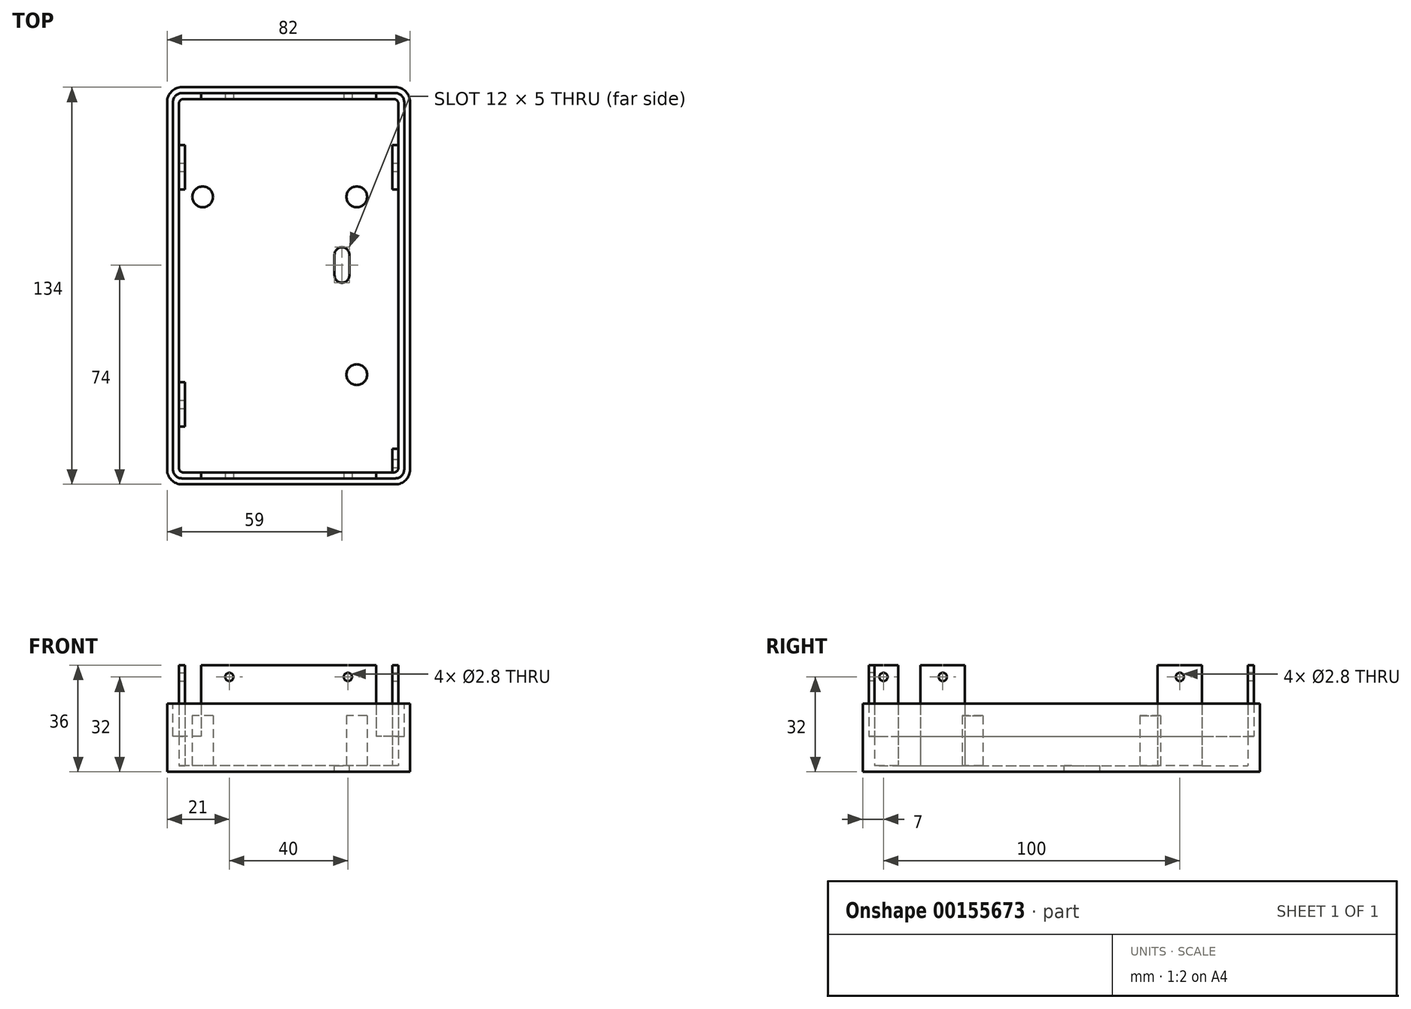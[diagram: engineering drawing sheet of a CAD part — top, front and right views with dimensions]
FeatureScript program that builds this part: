
annotation { "Feature Type Name" : "Feature", "Feature Type Description" : "" }
export const myFeature = defineFeature(function(context is Context, id is Id, definition is map)
    precondition{}
    {
        {
            var Q0;
            Q0=qCreatedBy(makeId("Top.planeOp"),FACE);
            var sketch = newSketch(context, id + "F0", { "sketchPlane" : qUnion([Q0])});
            skLineSegment(sketch, "E0.bottom", {"start": v(36, -67) * mm, "end": v(-36, -67) * mm});
            skLineSegment(sketch, "E0.top", {"start": v(36, 67) * mm, "end": v(-36, 67) * mm});
            skLineSegment(sketch, "E0.left", {"start": v(41, -62) * mm, "end": v(41, 62) * mm});
            skLineSegment(sketch, "E0.right", {"start": v(-41, -62) * mm, "end": v(-41, 62) * mm});
            skPoint(sketch, "E0.middle", {"position": v(0, 0) * mm});
            skPoint(sketch, "E1.visualSharp", {"position": v(-41, 67) * mm});
            skArc(sketch, "E1.filletArc", {"start": v(-36, 67) * mm, "mid": v(-39.54, 65.54) * mm, "end": v(-41, 62) * mm});
            skPoint(sketch, "E2.visualSharp", {"position": v(41, 67) * mm});
            skArc(sketch, "E2.filletArc", {"start": v(41, 62) * mm, "mid": v(39.54, 65.54) * mm, "end": v(36, 67) * mm});
            skPoint(sketch, "E3.visualSharp", {"position": v(41, -67) * mm});
            skArc(sketch, "E3.filletArc", {"start": v(36, -67) * mm, "mid": v(39.54, -65.54) * mm, "end": v(41, -62) * mm});
            skPoint(sketch, "E4.visualSharp", {"position": v(-41, -67) * mm});
            skArc(sketch, "E4.filletArc", {"start": v(-41, -62) * mm, "mid": v(-39.54, -65.54) * mm, "end": v(-36, -67) * mm});
            skSolve(sketch);
        }
        {
            var Q0;
            Q0=qSketchRegion(id+"F0",true);
            extrude(context, id + "F1", {"entities" : qUnion([Q0]), "depth" : 23 * mm});
        }
        {
            var Q0;
            Q0=makeQuery(id+"F1.opExtrude","CAP_FACE",FACE,{"disambiguationData":[OSD([sQuery(id+"F0.wireOp",EDGE,"E0.bottom"),sQuery(id+"F0.wireOp",EDGE,"E0.top"),sQuery(id+"F0.wireOp",EDGE,"E0.left"),sQuery(id+"F0.wireOp",EDGE,"E0.right"),sQuery(id+"F0.wireOp",EDGE,"E1.filletArc"),sQuery(id+"F0.wireOp",EDGE,"E2.filletArc"),sQuery(id+"F0.wireOp",EDGE,"E3.filletArc"),sQuery(id+"F0.wireOp",EDGE,"E4.filletArc")])],"isStart":false});
            shell(context, id + "F2", {"entities" : qUnion([Q0]), "thickness" : 2 * mm});
        }
        {
            var Q0;
            Q0=makeQuery(id+"F2.opShell","OFFSET_FACE",FACE,{"disambiguationData":[OSD([sQuery(id+"F0.wireOp",EDGE,"E0.bottom"),sQuery(id+"F0.wireOp",EDGE,"E0.top"),sQuery(id+"F0.wireOp",EDGE,"E0.left"),sQuery(id+"F0.wireOp",EDGE,"E0.right"),sQuery(id+"F0.wireOp",EDGE,"E1.filletArc"),sQuery(id+"F0.wireOp",EDGE,"E2.filletArc"),sQuery(id+"F0.wireOp",EDGE,"E3.filletArc"),sQuery(id+"F0.wireOp",EDGE,"E4.filletArc")])]});
            var sketch = newSketch(context, id + "F3", { "sketchPlane" : qUnion([Q0])});
            skCircle(sketch, "E5", {"center": v(-29, 30) * mm, "radius": 3.5 * mm});
            skCircle(sketch, "E6", {"center": v(23, 30) * mm, "radius": 3.5 * mm});
            skCircle(sketch, "E7", {"center": v(23, -30) * mm, "radius": 3.5 * mm});
            skLineSegment(sketch, "E8.left", {"start": v(20.5, 3.5) * mm, "end": v(20.5, 10.5) * mm});
            skLineSegment(sketch, "E8.right", {"start": v(15.5, 3.5) * mm, "end": v(15.5, 10.5) * mm});
            skPoint(sketch, "E8.middle", {"position": v(18, 7) * mm});
            skArc(sketch, "E9", {"start": v(15.5, 10.5) * mm, "mid": v(18, 13) * mm, "end": v(20.5, 10.5) * mm});
            skArc(sketch, "E10", {"start": v(20.5, 3.5) * mm, "mid": v(18, 1) * mm, "end": v(15.5, 3.5) * mm});
            skLineSegment(sketch, "E11.bottom", {"start": v(36, -65) * mm, "end": v(-36, -65) * mm});
            skLineSegment(sketch, "E11.top", {"start": v(36, 65) * mm, "end": v(-36, 65) * mm});
            skLineSegment(sketch, "E11.left", {"start": v(39, -62) * mm, "end": v(39, 62) * mm});
            skLineSegment(sketch, "E11.right", {"start": v(-39, -62) * mm, "end": v(-39, 62) * mm});
            skPoint(sketch, "E11.middle", {"position": v(0, 0) * mm});
            skLineSegment(sketch, "E12.bottom", {"start": v(35.5, -63) * mm, "end": v(-35.5, -63) * mm});
            skLineSegment(sketch, "E12.top", {"start": v(35.5, 63) * mm, "end": v(-35.5, 63) * mm});
            skLineSegment(sketch, "E12.left", {"start": v(37, -61.5) * mm, "end": v(37, 61.5) * mm});
            skLineSegment(sketch, "E12.right", {"start": v(-37, -61.5) * mm, "end": v(-37, 61.5) * mm});
            skPoint(sketch, "E13.visualSharp", {"position": v(-39, 65) * mm});
            skArc(sketch, "E13.filletArc", {"start": v(-36, 65) * mm, "mid": v(-38.12, 64.12) * mm, "end": v(-39, 62) * mm});
            skPoint(sketch, "E14.visualSharp", {"position": v(39, 65) * mm});
            skArc(sketch, "E14.filletArc", {"start": v(39, 62) * mm, "mid": v(38.12, 64.12) * mm, "end": v(36, 65) * mm});
            skPoint(sketch, "E15.visualSharp", {"position": v(39, -65) * mm});
            skArc(sketch, "E15.filletArc", {"start": v(36, -65) * mm, "mid": v(38.12, -64.12) * mm, "end": v(39, -62) * mm});
            skPoint(sketch, "E16.visualSharp", {"position": v(-39, -65) * mm});
            skArc(sketch, "E16.filletArc", {"start": v(-39, -62) * mm, "mid": v(-38.12, -64.12) * mm, "end": v(-36, -65) * mm});
            skPoint(sketch, "E17.visualSharp", {"position": v(-37, 63) * mm});
            skArc(sketch, "E17.filletArc", {"start": v(-35.5, 63) * mm, "mid": v(-36.56, 62.56) * mm, "end": v(-37, 61.5) * mm});
            skPoint(sketch, "E18.visualSharp", {"position": v(37, 63) * mm});
            skArc(sketch, "E18.filletArc", {"start": v(37, 61.5) * mm, "mid": v(36.56, 62.56) * mm, "end": v(35.5, 63) * mm});
            skPoint(sketch, "E19.visualSharp", {"position": v(37, -63) * mm});
            skArc(sketch, "E19.filletArc", {"start": v(35.5, -63) * mm, "mid": v(36.56, -62.56) * mm, "end": v(37, -61.5) * mm});
            skPoint(sketch, "E20.visualSharp", {"position": v(-37, -63) * mm});
            skArc(sketch, "E20.filletArc", {"start": v(-37, -61.5) * mm, "mid": v(-36.56, -62.56) * mm, "end": v(-35.5, -63) * mm});
            skSolve(sketch);
        }
        {
            var Q0;
            Q0=makeQuery(id+"F3.imprint","IMPRINT",FACE,{"disambiguationData":[TD([[makeQuery(id+"F3.imprint","IMPRINT",EDGE,{"derivedFrom":sQuery(id+"F3.wireOp",EDGE,"E5")}),1.0]])]});
            var Q1;
            Q1=makeQuery(id+"F3.imprint","IMPRINT",FACE,{"disambiguationData":[TD([[makeQuery(id+"F3.imprint","IMPRINT",EDGE,{"derivedFrom":sQuery(id+"F3.wireOp",EDGE,"E6")}),1.0]])]});
            var Q2;
            Q2=makeQuery(id+"F3.imprint","IMPRINT",FACE,{"disambiguationData":[TD([[makeQuery(id+"F3.imprint","IMPRINT",EDGE,{"derivedFrom":sQuery(id+"F3.wireOp",EDGE,"E7")}),1.0]])]});
            extrude(context, id + "F4", {"entities" : qUnion([Q0, Q1, Q2]), "operationType" : NewBodyOperationType.ADD, "depth" : 17 * mm});
        }
        {
            var Q0;
            Q0=makeQuery(id+"F3.imprint","IMPRINT",FACE,{"disambiguationData":[TD([[makeQuery(id+"F3.imprint","IMPRINT",EDGE,{"derivedFrom":sQuery(id+"F3.wireOp",EDGE,"E8.left")}),1.0]])]});
            extrude(context, id + "F5", {"entities" : qUnion([Q0]), "operationType" : NewBodyOperationType.REMOVE, "oppositeDirection" : true, "depth" : 2 * mm});
        }
        {
            var Q0;
            Q0=makeQuery(id+"F3.imprint","IMPRINT",FACE,{"disambiguationData":[TD([[makeQuery(id+"F3.imprint","IMPRINT",EDGE,{"derivedFrom":sQuery(id+"F3.wireOp",EDGE,"E11.bottom")}),-1.0]])]});
            extrude(context, id + "F6", {"entities" : qUnion([Q0]), "operationType" : NewBodyOperationType.ADD, "depth" : 10 * mm});
        }
        {
            var Q0;
            Q0=makeQuery(id+"F3.imprint","IMPRINT",FACE,{"disambiguationData":[TD([[makeQuery(id+"F3.imprint","IMPRINT",EDGE,{"derivedFrom":sQuery(id+"F3.wireOp",EDGE,"E5")}),-1.0]])]});
            var sketch = newSketch(context, id + "F7", { "sketchPlane" : qUnion([Q0])});
            skLineSegment(sketch, "E21.bottom", {"start": v(29.5, 63) * mm, "end": v(-29.5, 63) * mm});
            skLineSegment(sketch, "E21.top", {"start": v(29.5, 65) * mm, "end": v(-29.5, 65) * mm});
            skLineSegment(sketch, "E21.left", {"start": v(29.5, 63) * mm, "end": v(29.5, 65) * mm});
            skLineSegment(sketch, "E21.right", {"start": v(-29.5, 63) * mm, "end": v(-29.5, 65) * mm});
            skPoint(sketch, "E21.middle", {"position": v(0, 64) * mm});
            skLineSegment(sketch, "E22.bottom", {"start": v(29.5, -65) * mm, "end": v(-29.5, -65) * mm});
            skLineSegment(sketch, "E22.top", {"start": v(29.5, -63) * mm, "end": v(-29.5, -63) * mm});
            skLineSegment(sketch, "E22.left", {"start": v(29.5, -65) * mm, "end": v(29.5, -63) * mm});
            skLineSegment(sketch, "E22.right", {"start": v(-29.5, -65) * mm, "end": v(-29.5, -63) * mm});
            skPoint(sketch, "E22.middle", {"position": v(0, -64) * mm});
            skLineSegment(sketch, "E23.bottom", {"start": v(-37, 32.5) * mm, "end": v(-35, 32.5) * mm});
            skLineSegment(sketch, "E23.top", {"start": v(-37, 47.5) * mm, "end": v(-35, 47.5) * mm});
            skLineSegment(sketch, "E23.left", {"start": v(-37, 32.5) * mm, "end": v(-37, 47.5) * mm});
            skLineSegment(sketch, "E23.right", {"start": v(-35, 32.5) * mm, "end": v(-35, 47.5) * mm});
            skPoint(sketch, "E23.middle", {"position": v(-36, 40) * mm});
            skLineSegment(sketch, "E24.bottom", {"start": v(-37, -47.5) * mm, "end": v(-35, -47.5) * mm});
            skLineSegment(sketch, "E24.top", {"start": v(-37, -32.5) * mm, "end": v(-35, -32.5) * mm});
            skLineSegment(sketch, "E24.left", {"start": v(-37, -47.5) * mm, "end": v(-37, -32.5) * mm});
            skLineSegment(sketch, "E24.right", {"start": v(-35, -47.5) * mm, "end": v(-35, -32.5) * mm});
            skPoint(sketch, "E24.middle", {"position": v(-36, -40) * mm});
            skPoint(sketch, "E24.cornerSnap0", {"position": v(-37, 40) * mm});
            skLineSegment(sketch, "E25.bottom", {"start": v(37, 47.5) * mm, "end": v(35, 47.5) * mm});
            skLineSegment(sketch, "E25.top", {"start": v(37, 32.5) * mm, "end": v(35, 32.5) * mm});
            skLineSegment(sketch, "E25.left", {"start": v(37, 47.5) * mm, "end": v(37, 32.5) * mm});
            skLineSegment(sketch, "E25.right", {"start": v(35, 47.5) * mm, "end": v(35, 32.5) * mm});
            skPoint(sketch, "E25.middle", {"position": v(36, 40) * mm});
            skLineSegment(sketch, "E26.bottom", {"start": v(37, -55) * mm, "end": v(35, -55) * mm});
            skLineSegment(sketch, "E26.top", {"start": v(35.5, -63) * mm, "end": v(35, -63) * mm});
            skLineSegment(sketch, "E26.left", {"start": v(37, -55) * mm, "end": v(37, -61.5) * mm});
            skLineSegment(sketch, "E26.right", {"start": v(35, -55) * mm, "end": v(35, -63) * mm});
            skPoint(sketch, "E26.middle", {"position": v(36, -59) * mm});
            skPoint(sketch, "E27.visualSharp", {"position": v(37, -63) * mm});
            skArc(sketch, "E27.filletArc", {"start": v(35.5, -63) * mm, "mid": v(36.56, -62.56) * mm, "end": v(37, -61.5) * mm});
            skSolve(sketch);
        }
        {
            var Q0;
            Q0 = qSketchRegion(id + "F7", true);
            extrude(context, id + "F8", {"entities" : qUnion([Q0]), "operationType" : NewBodyOperationType.ADD, "depth" : 34 * mm});
        }
        {
            var Q0;
            Q0=makeQuery(id+"F8.opExtrude","SWEPT_FACE",FACE,{"disambiguationData":[OSD([sQuery(id+"F7.wireOp",EDGE,"E22.bottom")])]});
            var sketch = newSketch(context, id + "F9", { "sketchPlane" : qUnion([Q0])});
            skCircle(sketch, "E28", {"center": v(-20, 32) * mm, "radius": 1.4 * mm});
            skCircle(sketch, "E29", {"center": v(20, 32) * mm, "radius": 1.4 * mm});
            skSolve(sketch);
        }
        {
            var Q0;
            Q0 = qSketchRegion(id + "F9", true);
            extrude(context, id + "F10", {"entities" : qUnion([Q0]), "operationType" : NewBodyOperationType.REMOVE, "endBound" : BoundingType.THROUGH_ALL, "oppositeDirection" : true, "depth" : 25 * mm});
        }
        {
            var Q0;
            Q0=makeQuery(id+"F8.opExtrude","SWEPT_FACE",FACE,{"disambiguationData":[OSD([sQuery(id+"F7.wireOp",EDGE,"E25.left")])]});
            var sketch = newSketch(context, id + "F11", { "sketchPlane" : qUnion([Q0])});
            skCircle(sketch, "E30", {"center": v(40, 32) * mm, "radius": 1.4 * mm});
            skCircle(sketch, "E31", {"center": v(-40, 32) * mm, "radius": 1.4 * mm});
            skCircle(sketch, "E32", {"center": v(-60, 32) * mm, "radius": 1.4 * mm});
            skSolve(sketch);
        }
        {
            var Q0;
            Q0 = qSketchRegion(id + "F11", true);
            extrude(context, id + "F12", {"entities" : qUnion([Q0]), "operationType" : NewBodyOperationType.REMOVE, "endBound" : BoundingType.THROUGH_ALL, "oppositeDirection" : true, "depth" : 25 * mm});
        }
    });
